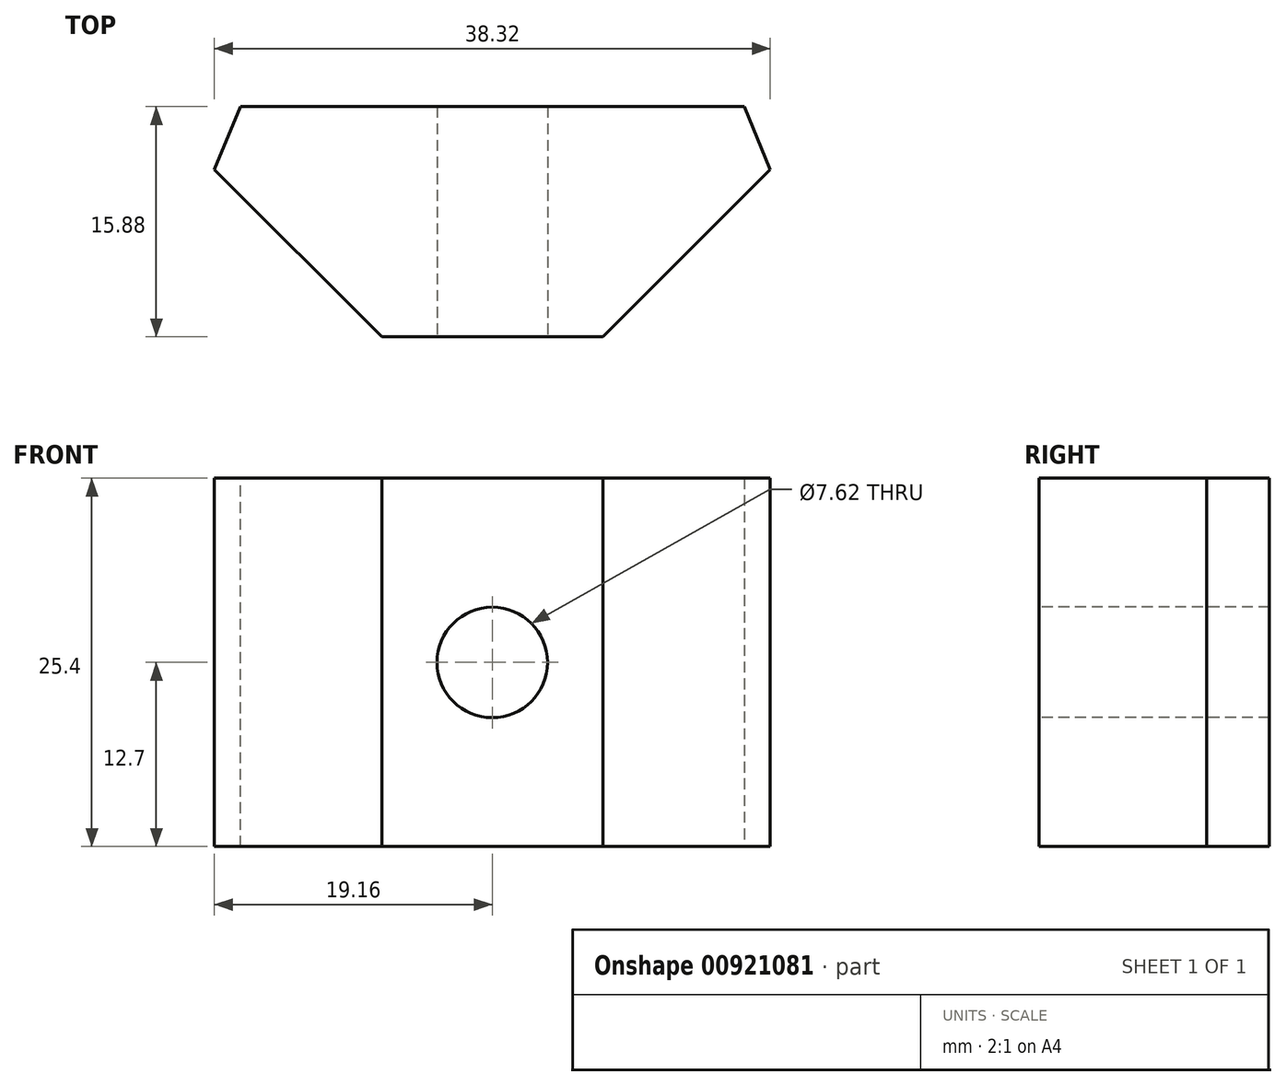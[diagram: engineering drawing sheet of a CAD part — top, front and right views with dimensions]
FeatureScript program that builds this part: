
annotation { "Feature Type Name" : "Feature", "Feature Type Description" : "" }
export const myFeature = defineFeature(function(context is Context, id is Id, definition is map)
    precondition{}
    {
        {
            var Q0;
            Q0=qCreatedBy(makeId("Top.planeOp"),FACE);
            var sketch = newSketch(context, id + "F0", { "sketchPlane" : qUnion([Q0])});
            skLineSegment(sketch, "E0", {"start": v(-7.62, 0) * mm, "end": v(7.62, 0) * mm});
            skLineSegment(sketch, "E1", {"start": v(7.62, 0) * mm, "end": v(23.5, 15.87) * mm});
            skLineSegment(sketch, "E2", {"start": v(23.5, 15.88) * mm, "end": v(-23.5, 15.88) * mm});
            skLineSegment(sketch, "E3", {"start": v(-23.5, 15.88) * mm, "end": v(-7.62, 0) * mm});
            skSolve(sketch);
        }
        {
            var Q0;
            Q0 = qSketchRegion(id + "F0", true);
            extrude(context, id + "F1", {"entities" : qUnion([Q0]), "endBound" : BoundingType.SYMMETRIC, "depth" : 25.4 * mm, "offsetDistance" : 25.4 * mm});
        }
        {
            var Q0;
            Q0=qCreatedBy(makeId("Front.planeOp"),FACE);
            var sketch = newSketch(context, id + "F2", { "sketchPlane" : qUnion([Q0])});
            skCircle(sketch, "E4", {"center": v(0, 0) * mm, "radius": 3.8 * mm});
            skSolve(sketch);
        }
        {
            var Q0;
            Q0 = qSketchRegion(id + "F2", true);
            extrude(context, id + "F3", {"entities" : qUnion([Q0]), "operationType" : NewBodyOperationType.REMOVE, "endBound" : BoundingType.THROUGH_ALL, "oppositeDirection" : true, "depth" : 25.4 * mm, "offsetDistance" : 25.4 * mm});
        }
        {
            var Q0;
            Q0=makeQuery(id+"F1.opExtrude","SWEPT_EDGE",EDGE,{"disambiguationData":[OSD([sQuery(id+"F0.wireOp",EDGE,"E2"),sQuery(id+"F0.wireOp",EDGE,"E3")])]});
            var Q1;
            Q1=makeQuery(id+"F1.opExtrude","SWEPT_EDGE",EDGE,{"disambiguationData":[OSD([sQuery(id+"F0.wireOp",EDGE,"E1"),sQuery(id+"F0.wireOp",EDGE,"E2")])]});
            chamfer(context, id + "F4", {"entities" : qUnion([Q0, Q1]), "width" : 2.54 * mm, "tangentPropagation" : true});
        }
    });
